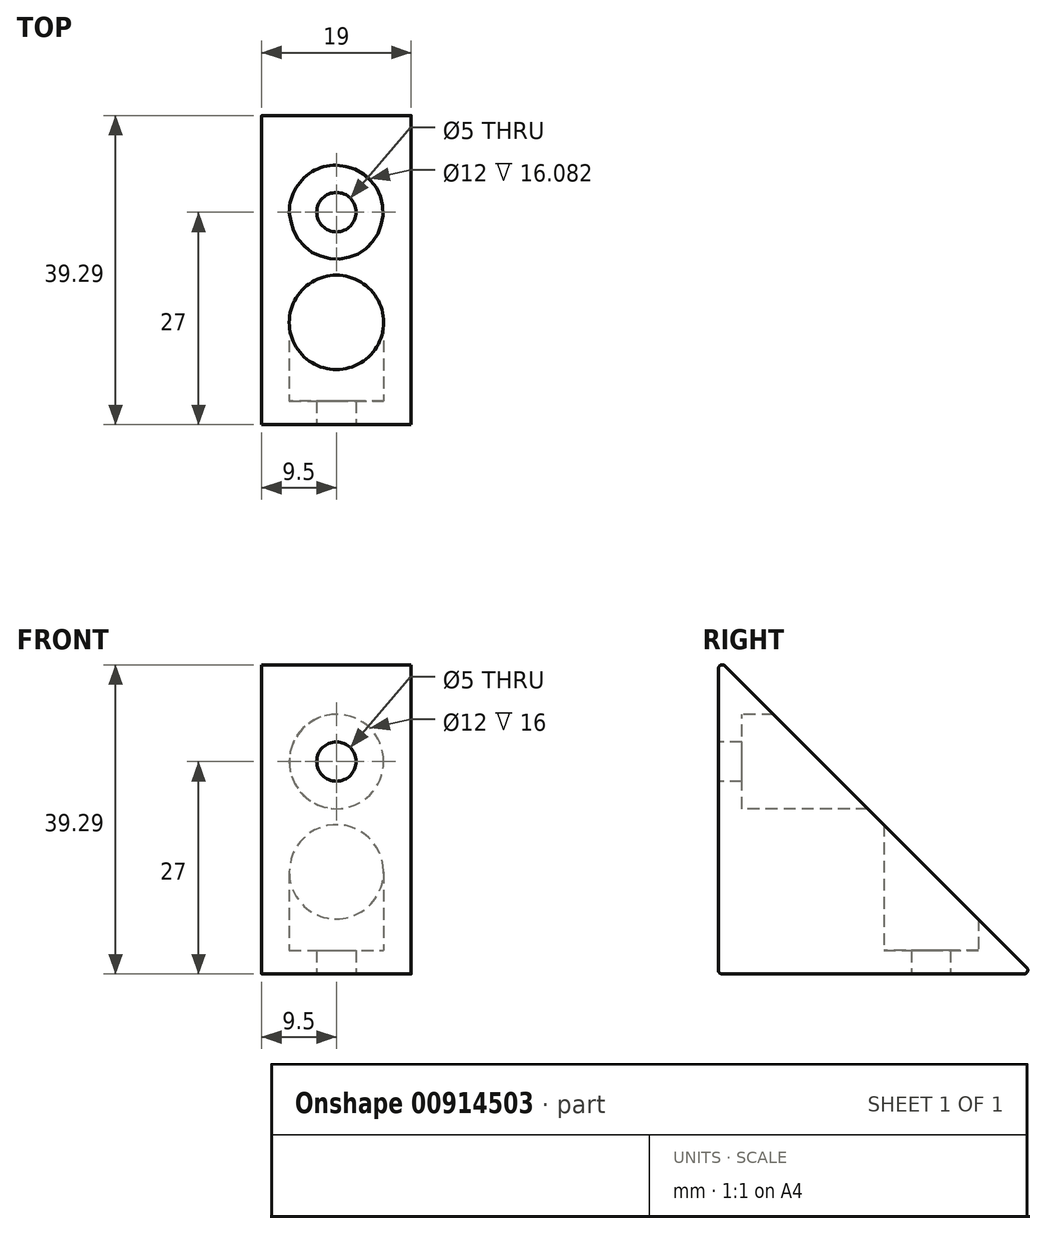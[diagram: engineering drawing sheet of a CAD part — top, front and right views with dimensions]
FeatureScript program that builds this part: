
annotation { "Feature Type Name" : "Feature", "Feature Type Description" : "" }
export const myFeature = defineFeature(function(context is Context, id is Id, definition is map)
    precondition{}
    {
        {
            var Q0;
            Q0=qCreatedBy(makeId("Front.planeOp"),FACE);
            var sketch = newSketch(context, id + "F0", { "sketchPlane" : qUnion([Q0])});
            skLineSegment(sketch, "E0.bottom", {"start": v(-9.5, 20) * mm, "end": v(9.5, 20) * mm});
            skLineSegment(sketch, "E0.top", {"start": v(-9.5, -20) * mm, "end": v(9.5, -20) * mm});
            skLineSegment(sketch, "E0.left", {"start": v(-9.5, 20) * mm, "end": v(-9.5, -20) * mm});
            skLineSegment(sketch, "E0.right", {"start": v(9.5, 20) * mm, "end": v(9.5, -20) * mm});
            skPoint(sketch, "E0.middle", {"position": v(0, 0) * mm});
            skSolve(sketch);
        }
        {
            var Q0;
            Q0=qSketchRegion(id+"F0",true);
            extrude(context, id + "F1", {"entities" : qUnion([Q0]), "depth" : 40 * mm, "offsetDistance" : 25 * mm});
        }
        {
            var Q0;
            Q0=makeQuery(id+"F1.opExtrude","SWEPT_FACE",FACE,{"disambiguationData":[OSD([sQuery(id+"F0.wireOp",EDGE,"E0.right")])]});
            var sketch = newSketch(context, id + "F2", { "sketchPlane" : qUnion([Q0])});
            skLineSegment(sketch, "E1", {"start": v(-40, 20) * mm, "end": v(0, -20) * mm});
            skLineSegment(sketch, "E2", {"start": v(0, -20) * mm, "end": v(0, 20) * mm});
            skLineSegment(sketch, "E3", {"start": v(0, 20) * mm, "end": v(-40, 20) * mm});
            skSolve(sketch);
        }
        {
            var Q0;
            Q0=qSketchRegion(id+"F2",true);
            extrude(context, id + "F3", {"entities" : qUnion([Q0]), "operationType" : NewBodyOperationType.REMOVE, "oppositeDirection" : true, "depth" : 25 * mm, "offsetDistance" : 25 * mm});
        }
        {
            var Q0;
            Q0=makeQuery(id+"F1.opExtrude","CAP_FACE",FACE,{"disambiguationData":[OSD([sQuery(id+"F0.wireOp",EDGE,"E0.bottom"),sQuery(id+"F0.wireOp",EDGE,"E0.top"),sQuery(id+"F0.wireOp",EDGE,"E0.left"),sQuery(id+"F0.wireOp",EDGE,"E0.right")])],"isStart":false});
            var sketch = newSketch(context, id + "F4", { "sketchPlane" : qUnion([Q0])});
            skCircle(sketch, "E4", {"center": v(0, 7) * mm, "radius": 2.5 * mm});
            skPoint(sketch, "E4.centerSnap0", {"position": v(0, 20) * mm});
            skSolve(sketch);
        }
        {
            var Q0;
            Q0 = qSketchRegion(id + "F4", true);
            extrude(context, id + "F5", {"entities" : qUnion([Q0]), "operationType" : NewBodyOperationType.REMOVE, "oppositeDirection" : true, "depth" : 25 * mm, "offsetDistance" : 25 * mm});
        }
        {
            var Q0;
            Q0=makeQuery(id+"F1.opExtrude","CAP_FACE",FACE,{"disambiguationData":[OSD([sQuery(id+"F0.wireOp",EDGE,"E0.bottom"),sQuery(id+"F0.wireOp",EDGE,"E0.top"),sQuery(id+"F0.wireOp",EDGE,"E0.left"),sQuery(id+"F0.wireOp",EDGE,"E0.right")])],"isStart":false});
            var sketch = newSketch(context, id + "F6", { "sketchPlane" : qUnion([Q0])});
            skCircle(sketch, "E5", {"center": v(0, 7) * mm, "radius": 6 * mm});
            skSolve(sketch);
        }
        {
            var Q0;
            Q0 = qSketchRegion(id + "F6", true);
            extrude(context, id + "F7", {"entities" : qUnion([Q0]), "operationType" : NewBodyOperationType.REMOVE, "oppositeDirection" : true, "depth" : 25 * mm, "offsetDistance" : 25 * mm, "hasSecondDirection" : true, "secondDirectionOppositeDirection" : true, "secondDirectionDepth" : 3 * mm});
        }
        {
            var Q0;
            Q0=makeQuery(id+"F1.opExtrude","SWEPT_FACE",FACE,{"disambiguationData":[OSD([sQuery(id+"F0.wireOp",EDGE,"E0.top")])]});
            var sketch = newSketch(context, id + "F8", { "sketchPlane" : qUnion([Q0])});
            skCircle(sketch, "E6", {"center": v(0, 13) * mm, "radius": 2.5 * mm});
            skSolve(sketch);
        }
        {
            var Q0;
            Q0 = qSketchRegion(id + "F8", true);
            extrude(context, id + "F9", {"entities" : qUnion([Q0]), "operationType" : NewBodyOperationType.REMOVE, "oppositeDirection" : true, "depth" : 25 * mm, "offsetDistance" : 25 * mm});
        }
        {
            var Q0;
            Q0=makeQuery(id+"F1.opExtrude","SWEPT_FACE",FACE,{"disambiguationData":[OSD([sQuery(id+"F0.wireOp",EDGE,"E0.top")])]});
            var sketch = newSketch(context, id + "F10", { "sketchPlane" : qUnion([Q0])});
            skCircle(sketch, "E7", {"center": v(0, 13) * mm, "radius": 6 * mm});
            skSolve(sketch);
        }
        {
            var Q0;
            Q0 = qSketchRegion(id + "F10", true);
            extrude(context, id + "F11", {"entities" : qUnion([Q0]), "operationType" : NewBodyOperationType.REMOVE, "oppositeDirection" : true, "depth" : 25 * mm, "offsetDistance" : 25 * mm, "hasSecondDirection" : true, "secondDirectionOppositeDirection" : true, "secondDirectionDepth" : 3 * mm});
        }
        {
            var Q0;
            Q0=makeQuery(id+"F3.boolean.opBoolean","MERGE",EDGE,{"derivedFrom":[makeQuery(id+"F1.opExtrude","CAP_EDGE",EDGE,{"disambiguationData":[OSD([sQuery(id+"F0.wireOp",EDGE,"E0.bottom")])],"isStart":false})],"fromTools":[makeQuery(id+"F3.opExtrude","SWEPT_EDGE",EDGE,{"disambiguationData":[OSD([sQuery(id+"F0.wireOp",EDGE,"E0.right"),sQuery(id+"F2.wireOp",EDGE,"E1"),sQuery(id+"F2.wireOp",EDGE,"E3")])]})]});
            var Q1;
            {var subQ0=sQuery(id+"F0.wireOp",EDGE,"E0.top");Q1=makeQuery(id+"F3.boolean.opBoolean","MERGE",EDGE,{"derivedFrom":[makeQuery(id+"F1.opExtrude","CAP_EDGE",EDGE,{"disambiguationData":[OSD([subQ0])],"isStart":true})],"fromTools":[makeQuery(id+"F3.opExtrude","SWEPT_EDGE",EDGE,{"disambiguationData":[OSD([subQ0,sQuery(id+"F0.wireOp",EDGE,"E0.right"),sQuery(id+"F2.wireOp",EDGE,"E1"),sQuery(id+"F2.wireOp",EDGE,"E2")])]})]});}
            var Q2;
            Q2=makeQuery(id+"F1.opExtrude","CAP_EDGE",EDGE,{"disambiguationData":[OSD([sQuery(id+"F0.wireOp",EDGE,"E0.top")])],"isStart":false});
            fillet(context, id + "F12", {"entities" : qUnion([Q0, Q1, Q2]), "radius" : .5 * mm, "tangentPropagation" : true, "allowEdgeOverflow" : false});
        }
    });
